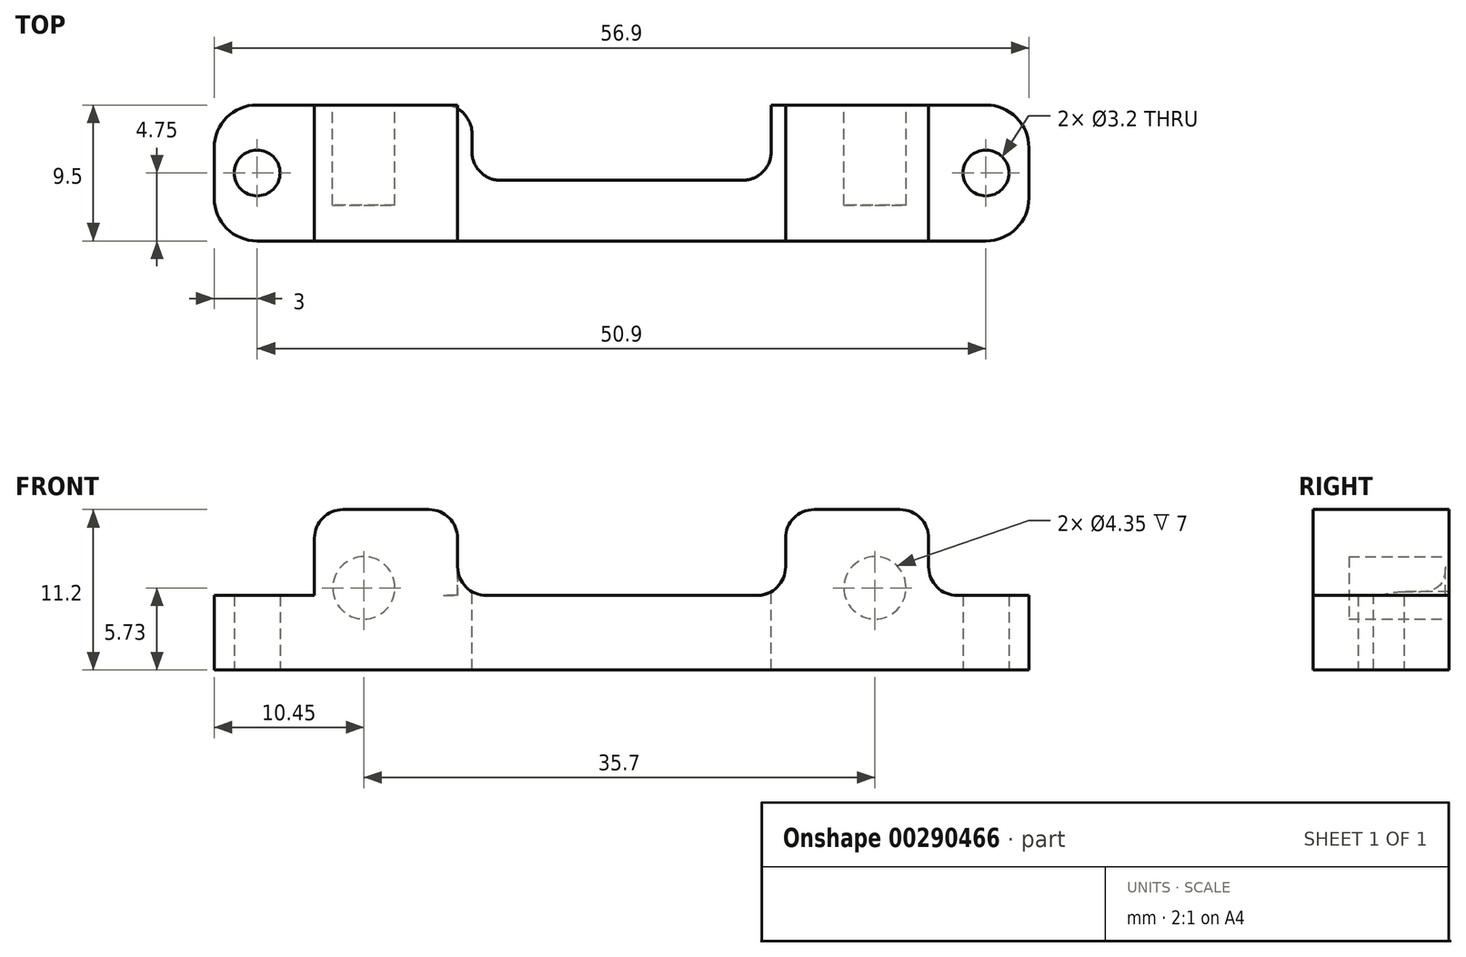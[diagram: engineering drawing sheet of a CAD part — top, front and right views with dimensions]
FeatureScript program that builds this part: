
annotation { "Feature Type Name" : "Feature", "Feature Type Description" : "" }
export const myFeature = defineFeature(function(context is Context, id is Id, definition is map)
    precondition{}
    {
        {
            var Q0;
            Q0=qCreatedBy(makeId("Top.planeOp"),FACE);
            var sketch = newSketch(context, id + "F0", { "sketchPlane" : qUnion([Q0])});
            skLineSegment(sketch, "E0.bottom", {"start": v(0, 0) * mm, "end": v(-57, 0) * mm});
            skLineSegment(sketch, "E0.top", {"start": v(-0.1, -9.5) * mm, "end": v(-57, -9.5) * mm});
            skLineSegment(sketch, "E0.left", {"start": v(-0.1, 0) * mm, "end": v(-0.1, -9.5) * mm});
            skLineSegment(sketch, "E0.right", {"start": v(-57, 0) * mm, "end": v(-57, -9.5) * mm});
            skPoint(sketch, "E1.centerSnap0", {"position": v(-57.36, -4.75) * mm});
            skCircle(sketch, "E2", {"center": v(-54, -4.75) * mm, "radius": 1.6 * mm});
            skCircle(sketch, "E3", {"center": v(-3.1, -4.75) * mm, "radius": 1.6 * mm});
            skSolve(sketch);
        }
        {
            var Q0;
            Q0=makeQuery(id+"F0.imprint","IMPRINT",FACE,{"disambiguationData":[TD([[makeQuery(id+"F0.imprint","IMPRINT",EDGE,{"derivedFrom":sQuery(id+"F0.wireOp",EDGE,"E0.top")}),-1.0]])]});
            extrude(context, id + "F1", {"entities" : qUnion([Q0]), "depth" : 5.2 * mm});
        }
        {
            var Q0;
            Q0=makeQuery(id+"F1.opExtrude","SWEPT_EDGE",EDGE,{"disambiguationData":[OSD([sQuery(id+"F0.wireOp",EDGE,"E0.top"),sQuery(id+"F0.wireOp",EDGE,"E0.right")])]});
            var Q1;
            Q1=makeQuery(id+"F1.opExtrude","SWEPT_EDGE",EDGE,{"disambiguationData":[OSD([sQuery(id+"F0.wireOp",EDGE,"E0.bottom"),sQuery(id+"F0.wireOp",EDGE,"E0.right")])]});
            var Q2;
            Q2=makeQuery(id+"F1.opExtrude","SWEPT_EDGE",EDGE,{"disambiguationData":[OSD([sQuery(id+"F0.wireOp",EDGE,"E0.top"),sQuery(id+"F0.wireOp",EDGE,"E0.left")])]});
            var Q3;
            Q3=makeQuery(id+"F1.opExtrude","SWEPT_EDGE",EDGE,{"disambiguationData":[OSD([sQuery(id+"F0.wireOp",EDGE,"E0.bottom"),sQuery(id+"F0.wireOp",EDGE,"E0.left")])]});
            fillet(context, id + "F2", {"entities" : qUnion([Q0, Q1, Q2, Q3]), "radius" : 3 * mm, "tangentPropagation" : true, "allowEdgeOverflow" : false});
        }
        {
            var Q0;
            Q0=makeQuery(id+"F1.opExtrude","CAP_FACE",FACE,{"disambiguationData":[OSD([sQuery(id+"F0.wireOp",EDGE,"E0.bottom"),sQuery(id+"F0.wireOp",EDGE,"E0.top"),sQuery(id+"F0.wireOp",EDGE,"E0.left"),sQuery(id+"F0.wireOp",EDGE,"E0.right"),sQuery(id+"F0.wireOp",EDGE,"E2"),sQuery(id+"F0.wireOp",EDGE,"E3")])],"isStart":false});
            var sketch = newSketch(context, id + "F3", { "sketchPlane" : qUnion([Q0])});
            skLineSegment(sketch, "E4.bottom", {"start": v(-39, 0) * mm, "end": v(-18.1, 0) * mm});
            skLineSegment(sketch, "E4.top", {"start": v(-39, -5.27) * mm, "end": v(-18.1, -5.27) * mm});
            skLineSegment(sketch, "E4.left", {"start": v(-39, 0) * mm, "end": v(-39, -5.27) * mm});
            skLineSegment(sketch, "E4.right", {"start": v(-18.1, 0) * mm, "end": v(-18.1, -5.27) * mm});
            skSolve(sketch);
        }
        {
            var Q0;
            Q0=makeQuery(id+"F3.imprint","IMPRINT",FACE,{"disambiguationData":[TD([[makeQuery(id+"F3.imprint","IMPRINT",EDGE,{"derivedFrom":sQuery(id+"F3.wireOp",EDGE,"E4.bottom")}),1.0]])]});
            extrude(context, id + "F4", {"entities" : qUnion([Q0]), "operationType" : NewBodyOperationType.REMOVE, "oppositeDirection" : true, "depth" : 25 * mm});
        }
        {
            var Q0;
            Q0=makeQuery(id+"F4.boolean.opBoolean","COPY",EDGE,{"derivedFrom":makeQuery(id+"F4.opExtrude","SWEPT_EDGE",EDGE,{"disambiguationData":[OSD([sQuery(id+"F3.wireOp",EDGE,"E4.top"),sQuery(id+"F3.wireOp",EDGE,"E4.left")])]})});
            var Q1;
            Q1=makeQuery(id+"F4.boolean.opBoolean","COPY",EDGE,{"derivedFrom":makeQuery(id+"F4.opExtrude","SWEPT_EDGE",EDGE,{"disambiguationData":[OSD([sQuery(id+"F0.wireOp",EDGE,"E0.bottom"),sQuery(id+"F3.wireOp",EDGE,"E4.bottom"),sQuery(id+"F3.wireOp",EDGE,"E4.left")])]})});
            var Q2;
            Q2=makeQuery(id+"F4.boolean.opBoolean","COPY",EDGE,{"derivedFrom":makeQuery(id+"F4.opExtrude","SWEPT_EDGE",EDGE,{"disambiguationData":[OSD([sQuery(id+"F3.wireOp",EDGE,"E4.top"),sQuery(id+"F3.wireOp",EDGE,"E4.right")])]})});
            var Q3;
            Q3=makeQuery(id+"F4.boolean.opBoolean","COPY",EDGE,{"derivedFrom":makeQuery(id+"F4.opExtrude","SWEPT_EDGE",EDGE,{"disambiguationData":[OSD([sQuery(id+"F0.wireOp",EDGE,"E0.bottom"),sQuery(id+"F3.wireOp",EDGE,"E4.bottom"),sQuery(id+"F3.wireOp",EDGE,"E4.right")])]})});
            fillet(context, id + "F5", {"entities" : qUnion([Q0, Q1, Q2, Q3]), "radius" : 2 * mm, "tangentPropagation" : true, "allowEdgeOverflow" : false});
        }
        {
            var Q0;
            Q0=makeQuery(id+"F1.opExtrude","CAP_FACE",FACE,{"disambiguationData":[OSD([sQuery(id+"F0.wireOp",EDGE,"E0.bottom"),sQuery(id+"F0.wireOp",EDGE,"E0.top"),sQuery(id+"F0.wireOp",EDGE,"E0.left"),sQuery(id+"F0.wireOp",EDGE,"E0.right"),sQuery(id+"F0.wireOp",EDGE,"E2"),sQuery(id+"F0.wireOp",EDGE,"E3")])],"isStart":false});
            var sketch = newSketch(context, id + "F6", { "sketchPlane" : qUnion([Q0])});
            skLineSegment(sketch, "E5.bottom", {"start": v(-50, 0) * mm, "end": v(-40, 0) * mm});
            skLineSegment(sketch, "E5.top", {"start": v(-50, -9.5) * mm, "end": v(-40, -9.5) * mm});
            skLineSegment(sketch, "E5.left", {"start": v(-50, 0) * mm, "end": v(-50, -9.5) * mm});
            skLineSegment(sketch, "E5.right", {"start": v(-40, 0) * mm, "end": v(-40, -9.5) * mm});
            skLineSegment(sketch, "E6.bottom", {"start": v(-16.1, 0) * mm, "end": v(-7.1, 0) * mm});
            skLineSegment(sketch, "E6.top", {"start": v(-17.1, -9.5) * mm, "end": v(-7.1, -9.5) * mm});
            skLineSegment(sketch, "E6.left", {"start": v(-17.1, 0) * mm, "end": v(-17.1, -9.5) * mm});
            skLineSegment(sketch, "E6.right", {"start": v(-7.1, 0) * mm, "end": v(-7.1, -9.5) * mm});
            skSolve(sketch);
        }
        {
            var Q0;
            {var subQ0=sQuery(id+"F6.wireOp",EDGE,"E5.bottom");var subQ4=sQuery(id+"F6.wireOp",EDGE,"E5.right");var subQ5=makeQuery(id+"F6.imprint","INTERSECT",VERTEX,{"derivedFrom":[subQ0,subQ4]});Q0=makeQuery(id+"F6.imprint","IMPRINT",FACE,{"disambiguationData":[TD([[makeQuery(id+"F6.imprint","IMPRINT",EDGE,{"disambiguationData":[TD([[subQ5,1.0]])],"derivedFrom":subQ0}),-1.0]])]});}
            var Q1;
            {var subQ6=sQuery(id+"F6.wireOp",EDGE,"E6.bottom");Q1=makeQuery(id+"F6.imprint","IMPRINT",FACE,{"disambiguationData":[TD([[makeQuery(id+"F6.imprint","IMPRINT",EDGE,{"derivedFrom":subQ6}),1.0]])]});}
            var Q2;
            {var subQ1=sQuery(id+"F6.wireOp",EDGE,"E5.top");Q2=makeQuery(id+"F6.imprint","IMPRINT",FACE,{"disambiguationData":[TD([[makeQuery(id+"F6.imprint","IMPRINT",EDGE,{"derivedFrom":subQ1}),-1.0]])]});}
            extrude(context, id + "F7", {"entities" : qUnion([Q0, Q1, Q2]), "operationType" : NewBodyOperationType.ADD, "depth" : 6 * mm});
        }
        {
            var Q0;
            Q0=makeQuery(id+"F7.opExtrude","CAP_EDGE",EDGE,{"disambiguationData":[OSD([sQuery(id+"F6.wireOp",EDGE,"E5.left")])],"isStart":false});
            var Q1;
            Q1=makeQuery(id+"F7.opExtrude","CAP_EDGE",EDGE,{"disambiguationData":[OSD([sQuery(id+"F6.wireOp",EDGE,"E5.right")])],"isStart":false});
            var Q2;
            {var subQ0=sQuery(id+"F6.wireOp",EDGE,"E5.right");Q2=makeQuery(id+"F7.boolean.opBoolean","SPLIT",EDGE,{"disambiguationData":[topologyDisambiguationEdgeConnected([makeQuery(id+"F1.opExtrude","CAP_FACE",FACE,{"disambiguationData":[OSD([sQuery(id+"F0.wireOp",EDGE,"E0.bottom"),sQuery(id+"F0.wireOp",EDGE,"E0.top"),sQuery(id+"F0.wireOp",EDGE,"E0.left"),sQuery(id+"F0.wireOp",EDGE,"E0.right"),sQuery(id+"F0.wireOp",EDGE,"E2"),sQuery(id+"F0.wireOp",EDGE,"E3")])],"isStart":false})])],"derivedFrom":makeQuery(id+"F7.opExtrude","CAP_EDGE",EDGE,{"disambiguationData":[OSD([subQ0])],"isStart":true})});}
            var Q3;
            Q3=makeQuery(id+"F7.opExtrude","CAP_EDGE",EDGE,{"disambiguationData":[OSD([sQuery(id+"F6.wireOp",EDGE,"E6.left")])],"isStart":true});
            var Q4;
            Q4=makeQuery(id+"F7.opExtrude","CAP_EDGE",EDGE,{"disambiguationData":[OSD([sQuery(id+"F6.wireOp",EDGE,"E5.left")])],"isStart":true});
            var Q5;
            Q5=makeQuery(id+"F7.opExtrude","CAP_EDGE",EDGE,{"disambiguationData":[OSD([sQuery(id+"F6.wireOp",EDGE,"E6.left")])],"isStart":false});
            var Q6;
            Q6=makeQuery(id+"F7.opExtrude","CAP_EDGE",EDGE,{"disambiguationData":[OSD([sQuery(id+"F6.wireOp",EDGE,"E6.right")])],"isStart":false});
            var Q7;
            Q7=makeQuery(id+"F7.opExtrude","CAP_EDGE",EDGE,{"disambiguationData":[OSD([sQuery(id+"F6.wireOp",EDGE,"E6.right")])],"isStart":true});
            fillet(context, id + "F8", {"entities" : qUnion([Q0, Q1, Q2, Q3, Q4, Q5, Q6, Q7]), "radius" : 2 * mm, "tangentPropagation" : true, "allowEdgeOverflow" : false});
        }
        {
            var Q0;
            {var subQ5=sQuery(id+"F0.wireOp",EDGE,"E0.bottom");Q0=makeQuery(id+"F7.boolean.opBoolean","MERGE",FACE,{"derivedFrom":[makeQuery(id+"F4.boolean.opBoolean","SPLIT",FACE,{"disambiguationData":[TD([makeQuery(id+"F4.opExtrude","SWEPT_FACE",FACE,{"disambiguationData":[OSD([sQuery(id+"F3.wireOp",EDGE,"E4.right")])]})])],"derivedFrom":makeQuery(id+"F1.opExtrude","SWEPT_FACE",FACE,{"disambiguationData":[OSD([subQ5])]})}),makeQuery(id+"F7.opExtrude","SWEPT_FACE",FACE,{"disambiguationData":[OSD([sQuery(id+"F6.wireOp",EDGE,"E6.bottom")])]})]});}
            var sketch = newSketch(context, id + "F9", { "sketchPlane" : qUnion([Q0])});
            skCircle(sketch, "E7", {"center": v(10.85, 5.73) * mm, "radius": 2.17 * mm});
            skCircle(sketch, "E8", {"center": v(46.55, 5.73) * mm, "radius": 2.17 * mm});
            skSolve(sketch);
        }
        {
            var Q0;
            Q0=makeQuery(id+"F9.imprint","IMPRINT",FACE,{"disambiguationData":[TD([[makeQuery(id+"F9.imprint","IMPRINT",EDGE,{"derivedFrom":sQuery(id+"F9.wireOp",EDGE,"E7")}),1.0]])]});
            var Q1;
            Q1=makeQuery(id+"F9.imprint","IMPRINT",FACE,{"disambiguationData":[TD([[makeQuery(id+"F9.imprint","IMPRINT",EDGE,{"derivedFrom":sQuery(id+"F9.wireOp",EDGE,"E8")}),1.0]])]});
            extrude(context, id + "F10", {"entities" : qUnion([Q0, Q1]), "operationType" : NewBodyOperationType.REMOVE, "oppositeDirection" : true, "depth" : 7 * mm});
        }
    });
